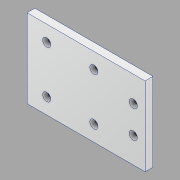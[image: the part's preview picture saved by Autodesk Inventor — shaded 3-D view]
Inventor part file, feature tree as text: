
AUTODESK INVENTOR PART (.ipt)
format: ipt  version: 2020 (Build 240168000, 168)  size: 112,128 bytes
history: native  units: in
note: dims shown in document units (in); Inventor stores cm internally (conversion verified against a paired STEP export)
features: sketch x2, other x1, extrude x1, hole x1
ambient origin geometry x8: Origin, YZ Plane, XZ Plane, XY Plane, X Axis, Y Axis, Z Axis, Center Point
bodies: Body1 (feature_tree)
feature tree (5):
  other  "Sólido1"
  extrude  "Extrusión1"  Depth=2.5in
  hole  "Agujero1"  [1 undecoded]
  sketch  "Boceto1"  dims[d0=3.75in d1=2.5in]
  sketch  "Boceto2"  dims[d2=0.25in d3=0.0in d4=0.375in d5=1.25in d6=1.5in d7=0.375in d8=1.25in d9=1.5in d10=2.5in d11=1.25in d12=0.875in d13=0.4375in d14=1.5in d15=1.5in d16=0.75in d17=0.75in d18=0.0979in d19=0.25in d20=0.26in d21=0.0118in d22=0.5635in d23=0.375in d24=0.8108in]
note: 1 required parameter value undecoded (feature->parameter linkage not recoverable at this tier; creation-order binding heuristic only, values carry confidence <= 0.55)
